# Revit family: LSER22
name_source: partatom
category: Lighting Fixtures
units: mm (PartAtom-declared; Revit-internal decimal feet)

## family parameters
Cut with Voids When Loaded = No
Host = Face
Light Source = Yes
Part Type = Normal
Room Calculation Point = No
Round Connector Dimension = Use Diameter
Shared = No

## types (24) — shared parameters
Apparent Load = 0 VA
Body = Paint White
Color Filter = 16777215
Default Elevation = 4' - 0"
Dimming Lamp Color Temperature Shift = <None>
LEGNTH = 4' - 6"
Manufacturer = COLUMBIA
Model = LSER22
Number of Poles = 1
Power Factor = 1
Tilt Angle = 90.00°
Voltage = 0 V
WIDTH = 2' - 0"

## per-type parameters (varying)
| type | Photometric Web File | URL |
| LSER22-30HLG-C-ESD | itl78367.ies | https://www.currentlighting.com |
| LSER22-30HLG-R-ESD | itl78368.ies | https://www.currentlighting.com |
| LSER22-30LWG-C-ESD | itl78371.ies | https://www.currentlighting.com |
| LSER22-30LWG-R-ESD | itl78372.ies | https://www.currentlighting.com |
| LSER22-30MLG-C-ESD | itl78353.ies | https://www.currentlighting.com |
| LSER22-30MLG-R-ESD | itl78356.ies | https://www.currentlighting.com |
| LSER22-30VLG-C-ESD | itl78369.ies | https://www.currentlighting.com |
| LSER22-30VLG-R-ESD | itl78370.ies | https://www.currentlighting.com |
| LSER22-35HLG-C-ESD | itl78359.ies | https://www.currentlighting.com |
| LSER22-35HLG-R-ESD | itl78361.ies | https://www.currentlighting.com |
| LSER22-35LWG-C-ESD | itl78349.ies | https://www.currentlighting.com |
| LSER22-35LWG-R-ESD | itl78351.ies | https://www.currentlighting.com |
| LSER22-35MLG-C-ESD | itl78354.ies | https://www.currentlighting.com |
| LSER22-35MLG-R-ESD | itl78357.ies | https://www.currentlighting.com |
| LSER22-35VLG-C-ESD | itl78363.ies | https://www.currentlighting.com |
| LSER22-35VLG-R-ESD | itl78365.ies | https://www.currentlighting.com |
| LSER22-40HLG-C-ESD | itl78360.ies | https://www.currentlighting.com |
| LSER22-40HLG-R-ESD | itl78362.ies |  |
| LSER22-40LWG-C-ESD | itl78350.ies |  |
| LSER22-40LWG-R-ESD | itl78352.ies | https://www.currentlighting.com |
| LSER22-40MLG-C-ESD | itl78355.ies | https://www.currentlighting.com |
| LSER22-40MLG-R-ESD | itl78358.ies | https://www.currentlighting.com |
| LSER22-40VLG-C-ESD | itl78364.ies | https://www.currentlighting.com |
| LSER22-40VLG-R-ESD | itl78366.ies | https://www.currentlighting.com |

## geometry (parser evidence)
native form markers: Sweep x2
no freeform markers — native parametric forms only
